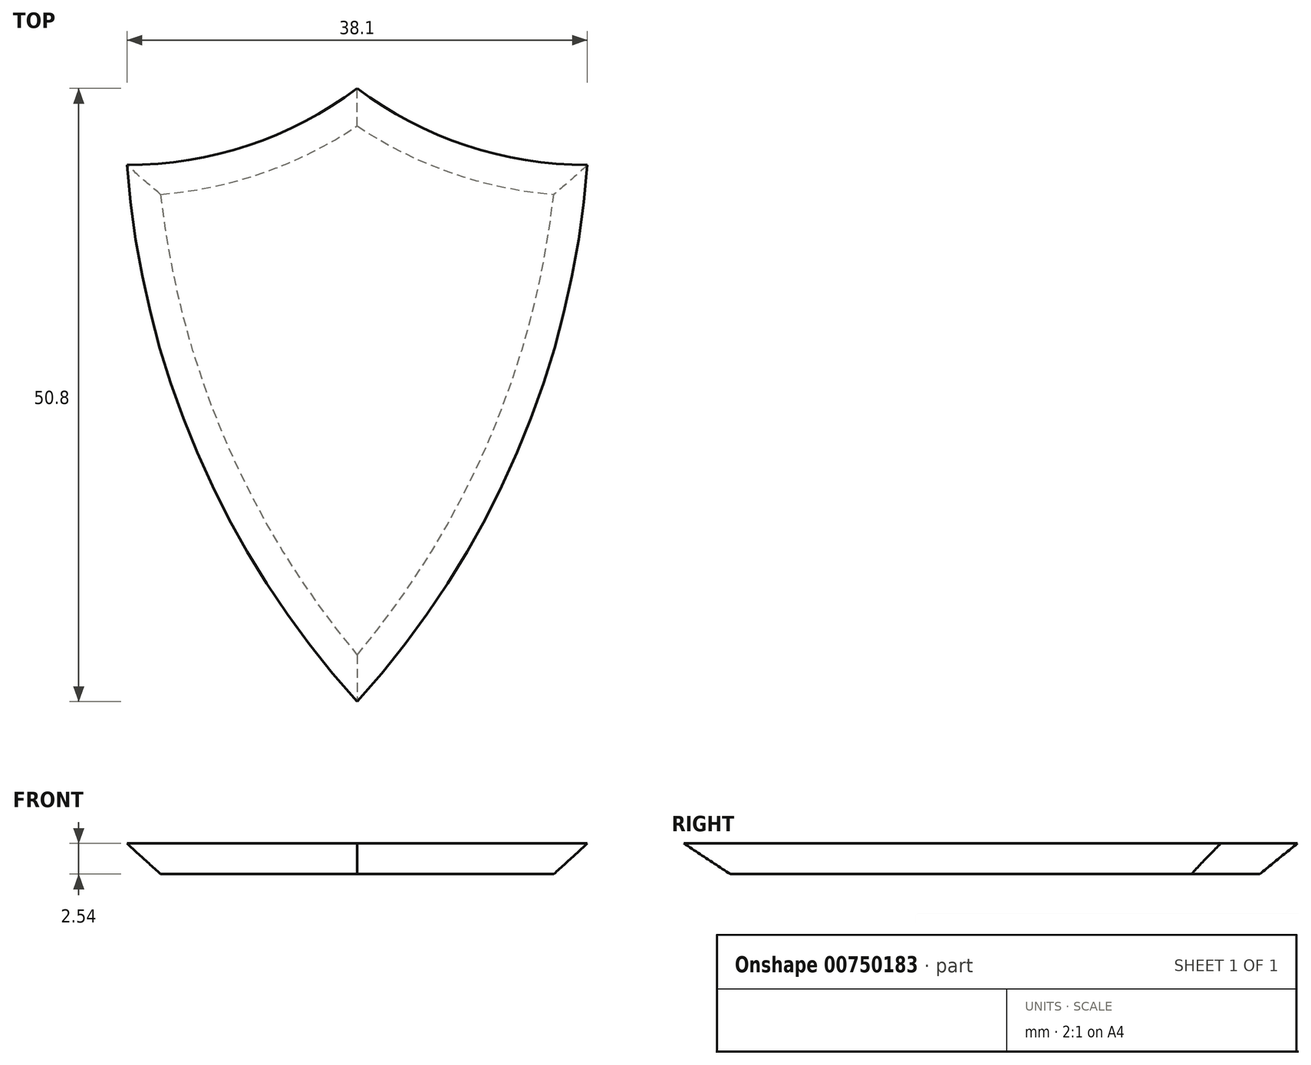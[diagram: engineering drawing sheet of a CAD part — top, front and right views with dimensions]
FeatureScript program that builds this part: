
annotation { "Feature Type Name" : "Feature", "Feature Type Description" : "" }
export const myFeature = defineFeature(function(context is Context, id is Id, definition is map)
    precondition{}
    {
        {
            var Q0;
            Q0=qCreatedBy(makeId("Top.planeOp"),FACE);
            var sketch = newSketch(context, id + "F0", { "sketchPlane" : qUnion([Q0])});
            skPoint(sketch, "E0.middle", {"position": v(0, 0) * mm});
            skArc(sketch, "E1", {"start": v(-19.05, 19.05) * mm, "mid": v(-9, 20.68) * mm, "end": v(0, 25.4) * mm});
            skArc(sketch, "E2", {"start": v(-19.05, 19.05) * mm, "mid": v(-13.24, -4.77) * mm, "end": v(0, -25.4) * mm});
            skArc(sketch, "E3.MirrorCS", {"start": v(19.05, 19.05) * mm, "mid": v(9, 20.68) * mm, "end": v(0, 25.4) * mm});
            skArc(sketch, "E4.MirrorCS", {"start": v(19.05, 19.05) * mm, "mid": v(13.24, -4.77) * mm, "end": v(0, -25.4) * mm});
            skSolve(sketch);
        }
        {
            var Q0;
            Q0=makeQuery(id+"F0.imprint","IMPRINT",FACE,{"disambiguationData":[TD([[makeQuery(id+"F0.imprint","IMPRINT",EDGE,{"derivedFrom":sQuery(id+"F0.wireOp",EDGE,"E1")}),-1.0]])]});
            extrude(context, id + "F1", {"entities" : qUnion([Q0]), "depth" : 2.54 * mm, "offsetDistance" : 25.4 * mm});
        }
        {
            var Q0;
            Q0=makeQuery(id+"F1.opExtrude","CAP_EDGE",EDGE,{"disambiguationData":[OSD([sQuery(id+"F0.wireOp",EDGE,"E4.MirrorCS")])],"isStart":true});
            var Q1;
            Q1=makeQuery(id+"F1.opExtrude","CAP_EDGE",EDGE,{"disambiguationData":[OSD([sQuery(id+"F0.wireOp",EDGE,"E2")])],"isStart":true});
            var Q2;
            Q2=makeQuery(id+"F1.opExtrude","CAP_EDGE",EDGE,{"disambiguationData":[OSD([sQuery(id+"F0.wireOp",EDGE,"E1")])],"isStart":true});
            var Q3;
            Q3=makeQuery(id+"F1.opExtrude","CAP_EDGE",EDGE,{"disambiguationData":[OSD([sQuery(id+"F0.wireOp",EDGE,"E3.MirrorCS")])],"isStart":true});
            chamfer(context, id + "F2", {"entities" : qUnion([Q0, Q1, Q2, Q3]), "width" : 2.54 * mm, "tangentPropagation" : true});
        }
    });
